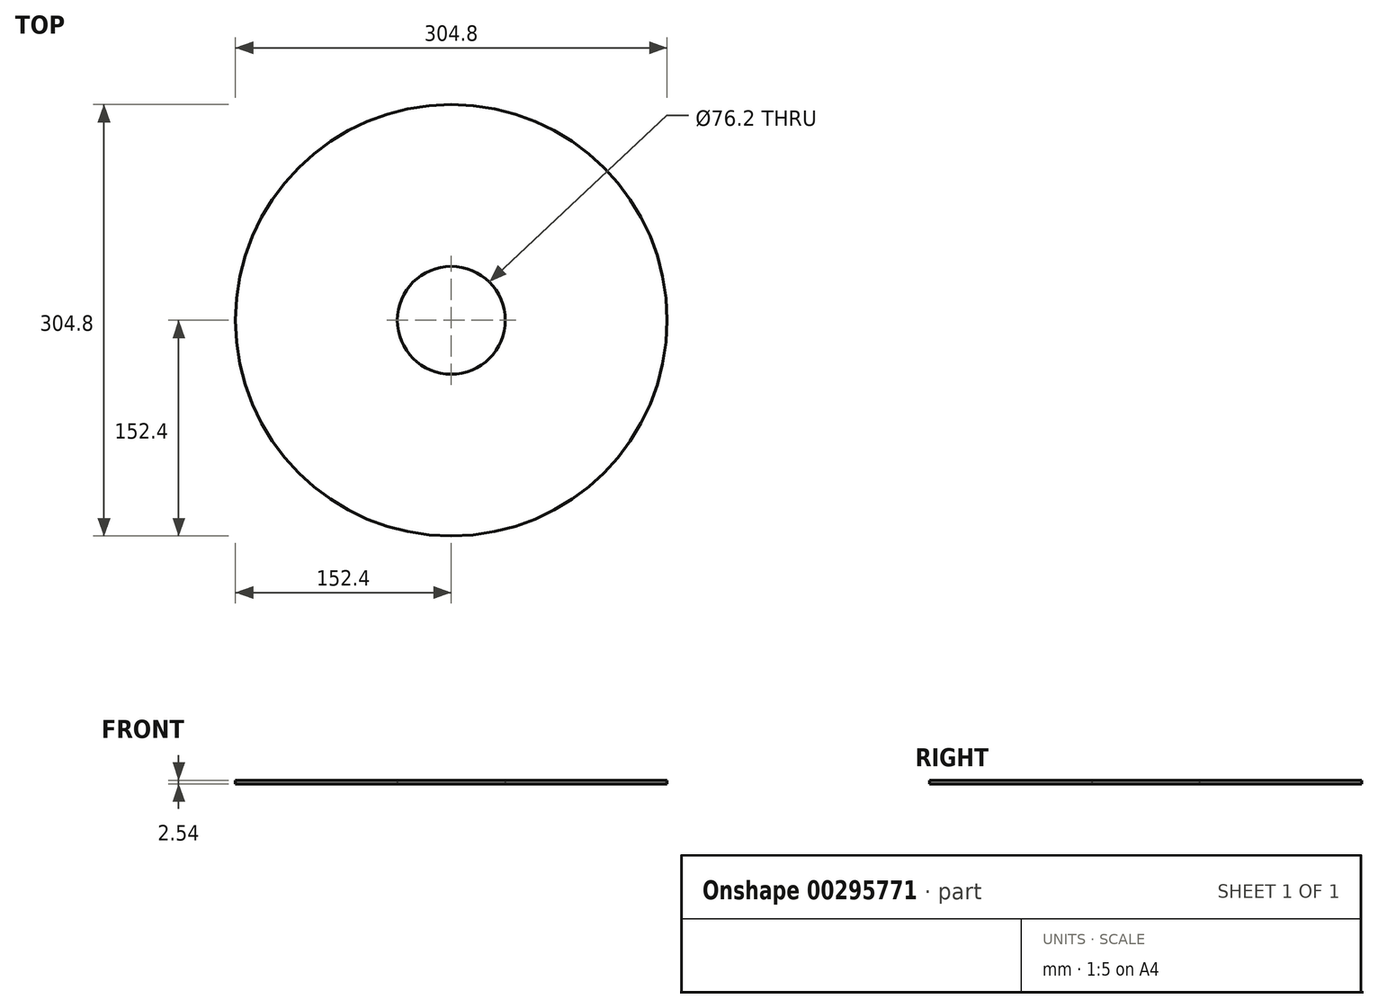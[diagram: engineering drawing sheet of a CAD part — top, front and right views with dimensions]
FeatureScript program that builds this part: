
annotation { "Feature Type Name" : "Feature", "Feature Type Description" : "" }
export const myFeature = defineFeature(function(context is Context, id is Id, definition is map)
    precondition{}
    {
        {
            var Q0;
            Q0=qCreatedBy(makeId("Top.planeOp"),FACE);
            var sketch = newSketch(context, id + "F0", { "sketchPlane" : qUnion([Q0])});
            skCircle(sketch, "E0", {"center": v(0, 0) * mm, "radius": 152.4 * mm});
            skCircle(sketch, "E1", {"center": v(0, 0) * mm, "radius": 38.1 * mm});
            skSolve(sketch);
        }
        {
            var Q0;
            Q0 = qSketchRegion(id + "F0", true);
            extrude(context, id + "F1", {"entities" : qUnion([Q0]), "depth" : 2.54 * mm});
        }
    });
